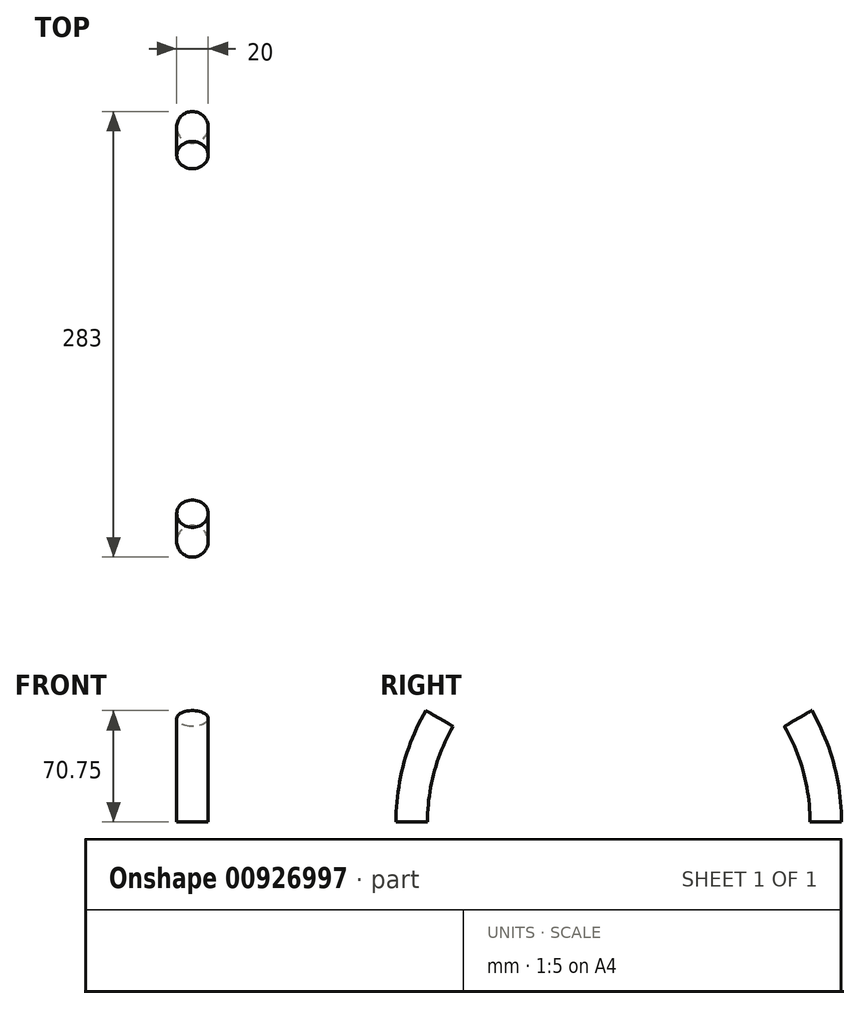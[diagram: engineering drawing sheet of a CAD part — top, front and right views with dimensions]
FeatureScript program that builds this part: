
annotation { "Feature Type Name" : "Feature", "Feature Type Description" : "" }
export const myFeature = defineFeature(function(context is Context, id is Id, definition is map)
    precondition{}
    {
        {
            var Q0;
            Q0=qCreatedBy(makeId("Top.planeOp"),FACE);
            var sketch = newSketch(context, id + "F0", { "sketchPlane" : qUnion([Q0])});
            skCircle(sketch, "E0", {"center": v(0, 131.5) * mm, "radius": 10 * mm});
            skCircle(sketch, "E1", {"center": v(0, -131.5) * mm, "radius": 10 * mm});
            skSolve(sketch);
        }
        {
            var Q0;
            Q0=qCreatedBy(makeId("Right.planeOp"),FACE);
            var sketch = newSketch(context, id + "F1", { "sketchPlane" : qUnion([Q0])});
            skLineSegment(sketch, "E2", {"start": v(-131.5, 0) * mm, "end": v(0, 0) * mm});
            skLineSegment(sketch, "E3", {"start": v(0, 0) * mm, "end": v(131.5, 0) * mm});
            skLineSegment(sketch, "E4", {"start": v(0, 0) * mm, "end": v(0, 263) * mm});
            skArc(sketch, "E5", {"start": v(131.5, 0) * mm, "mid": v(127.02, 34.03) * mm, "end": v(113.88, 65.75) * mm});
            skArc(sketch, "E6.trimOffspring", {"start": v(-113.88, 65.75) * mm, "mid": v(-127.02, 34.03) * mm, "end": v(-131.5, 0) * mm});
            skPoint(sketch, "E7.center.orphan", {"position": v(0, 131.5) * mm});
            skArc(sketch, "E8", {"start": v(113.88, 65.75) * mm, "mid": v(0, 131.5) * mm, "end": v(-113.88, 65.75) * mm});
            skArc(sketch, "E9", {"start": v(-131.5, 131.5) * mm, "mid": v(0, 0) * mm, "end": v(131.5, 131.5) * mm});
            skLineSegment(sketch, "E10", {"start": v(0, 131.5) * mm, "end": v(131.5, 131.5) * mm});
            skLineSegment(sketch, "E11", {"start": v(131.5, 131.5) * mm, "end": v(-131.5, 131.5) * mm});
            skSolve(sketch);
        }
        {
            var Q0;
            Q0=makeQuery(id+"F0.imprint","IMPRINT",FACE,{"disambiguationData":[TD([[makeQuery(id+"F0.imprint","IMPRINT",EDGE,{"derivedFrom":sQuery(id+"F0.wireOp",EDGE,"E1")}),1.0]])]});
            var Q1;
            Q1=sQuery(id+"F1.wireOp",EDGE,"E6.trimOffspring");
            sweep(context, id + "F2", {"profiles" : qUnion([Q0]), "path" : qUnion([Q1])});
        }
        {
            var Q0;
            Q0=makeQuery(id+"F0.imprint","IMPRINT",FACE,{"disambiguationData":[TD([[makeQuery(id+"F0.imprint","IMPRINT",EDGE,{"derivedFrom":sQuery(id+"F0.wireOp",EDGE,"E0")}),1.0]])]});
            var Q1;
            Q1=sQuery(id+"F1.wireOp",EDGE,"E5");
            sweep(context, id + "F3", {"profiles" : qUnion([Q0]), "path" : qUnion([Q1])});
        }
    });
